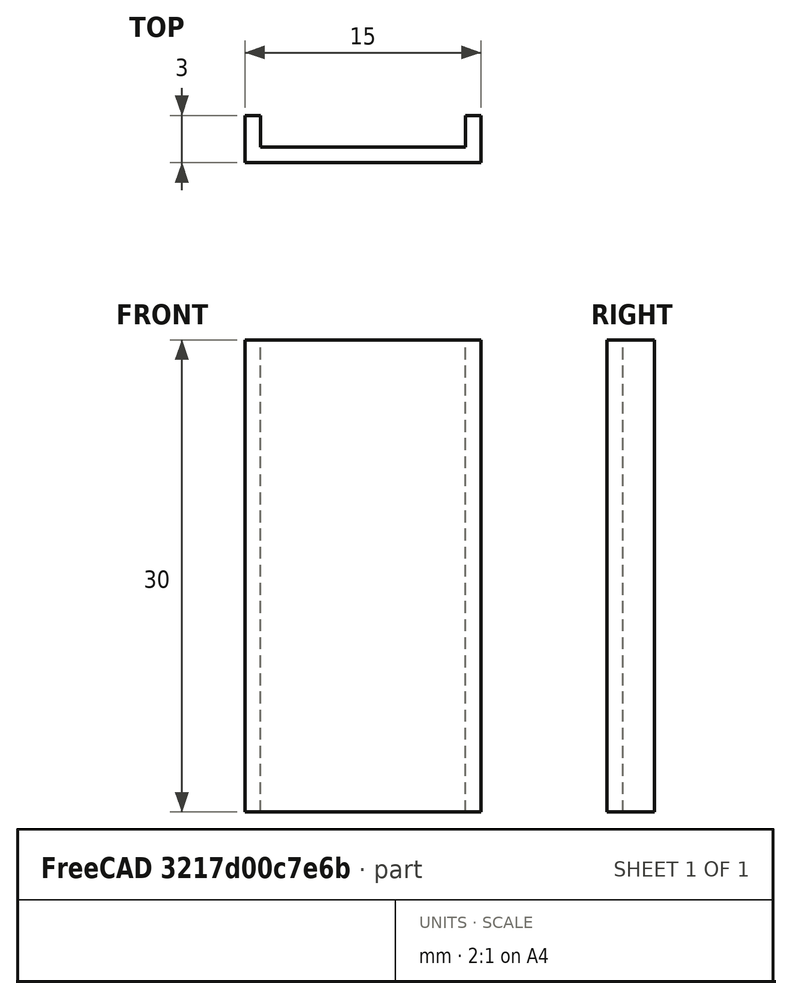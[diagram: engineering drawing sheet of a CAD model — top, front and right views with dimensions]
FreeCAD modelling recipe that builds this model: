
FCSTD DOCUMENT  (FreeCAD 0.16R6712 (Git))
Label: Aile_renfort_interne
License: All rights reserved
LicenseURL: http://en.wikipedia.org/wiki/All_rights_reserved
objects: Sketcher::SketchObject×1, PartDesign::Pad×1
note: 3 computed .brp shape members not serialized (recipe doc carries the construction recipe); baked Part::Feature solids carry a one-line shape summary decoded from their .brp

FEATURE [Sketcher::SketchObject] Sketch
  sketch-geometry (8):
    g0: LineSegment StartX=0 StartY=3 StartZ=0 EndX=0 EndY=0 EndZ=0
    g1: LineSegment StartX=0 StartY=0 StartZ=0 EndX=15 EndY=0 EndZ=0
    g2: LineSegment StartX=15 StartY=0 StartZ=0 EndX=15 EndY=3 EndZ=0
    g3: LineSegment StartX=15 StartY=3 StartZ=0 EndX=14 EndY=3 EndZ=0
    g4: LineSegment StartX=14 StartY=3 StartZ=0 EndX=14 EndY=1 EndZ=0
    g5: LineSegment StartX=14 StartY=1 StartZ=0 EndX=1 EndY=1 EndZ=0
    g6: LineSegment StartX=1 StartY=1 StartZ=0 EndX=1 EndY=3 EndZ=0
    g7: LineSegment StartX=1 StartY=3 StartZ=0 EndX=0 EndY=3 EndZ=0
  constraints (24):
    c: Coincident(g1,g0)
    c: PointOnObject(g1,g-1)
    c: Horizontal(g1)
    c: Coincident(g2,g1)
    c: Coincident(g3,g2)
    c: Horizontal(g3)
    c: Coincident(g4,g3)
    c: Vertical(g4)
    c: Coincident(g5,g4)
    c: Horizontal(g5)
    c: Coincident(g6,g5)
    c: Coincident(g7,g6)
    c: Coincident(g7,g0)
    c: Horizontal(g7)
    c: Vertical(g0)
    c: Vertical(g6)
    c: DistanceX(g3,g3) = 1
    c: Vertical(g2)
    c: DistanceX(g1,g1) = 15
    c: DistanceX(g7,g7) = 1
    c: Coincident(g0,g-1)
    c: DistanceY(g1,g4) = 1
    c: DistanceY(g2,g2) = 3
    c: DistanceY(g0,g0) = 3
FEATURE [PartDesign::Pad] Pad
  Length = 30
  Length2 = 100
  Sketch = -> Sketch
  Type = 0
